# Revit family: Cabinet-Pass_Through-Bobrick-Recessed_Specimen-B-505
name_source: partatom
category: Specialty Equipment
revit_build: Autodesk Revit 2016 (Build: 20150714_1515(x64)
units: mm (PartAtom-declared; Revit-internal decimal feet)

## family parameters
Cut with Voids When Loaded = No
Host = Face
OmniClass Number = 23.40.00.00
OmniClass Title = Equipment and Furnishings
Part Type = Normal
Room Calculation Point = No
Round Connector Dimension = Use Diameter
Shared = Yes

## types (1)
- B-505
    ATS URL = http://www.atsspec.net
    Assembly Code = E2010
    Default Elevation = 0"
    Description = B-505 Recessed Specimen Pass-Thru Cabinet
    Height = 12 1/16"
    Installation Type = Wall Mounted
    Length = 6"
    Manufacturer = Bobrick
    Material = Stainless Steel-Bobrick-Type 304-Satin
    Model = B-505
    Price = Prices may vary. Please consult Manufacturer Representative for most up-to-date price list.
    Product Documentation Link = https://www.bobrick.com
    Product Page URL = http://products.bobrick.com
    URL = http://www.bobrick.com
    Width = 12 3/4"

## geometry (parser evidence)
native form markers: Sweep x3
no freeform markers — native parametric forms only
